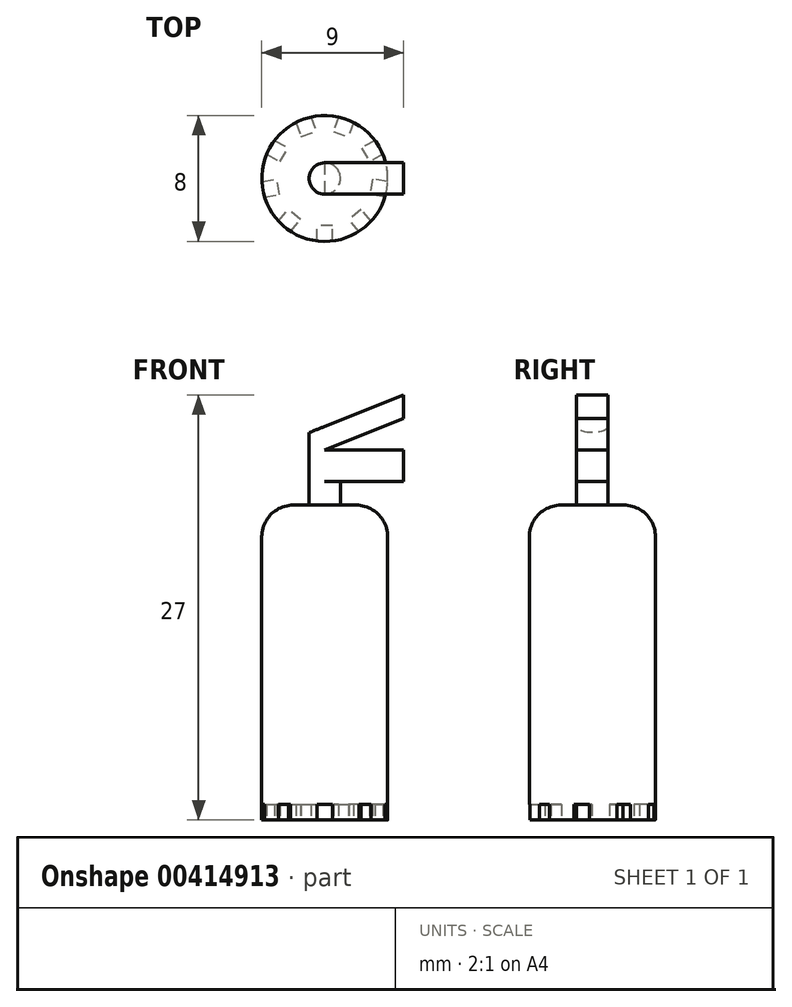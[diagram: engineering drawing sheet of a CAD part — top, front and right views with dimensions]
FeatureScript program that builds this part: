
annotation { "Feature Type Name" : "Feature", "Feature Type Description" : "" }
export const myFeature = defineFeature(function(context is Context, id is Id, definition is map)
    precondition{}
    {
        {
            var Q0;
            Q0=qCreatedBy(makeId("Top.planeOp"),FACE);
            var sketch = newSketch(context, id + "F0", { "sketchPlane" : qUnion([Q0])});
            skCircle(sketch, "E0", {"center": v(0, 0) * mm, "radius": 4 * mm});
            skSolve(sketch);
        }
        {
            var Q0;
            Q0 = qSketchRegion(id + "F0", true);
            extrude(context, id + "F1", {"entities" : qUnion([Q0]), "depth" : 20 * mm});
        }
        {
            var Q0;
            Q0=makeQuery(id+"F1.opExtrude","CAP_EDGE",EDGE,{"disambiguationData":[OSD([sQuery(id+"F0.wireOp",EDGE,"E0")])],"isStart":false});
            fillet(context, id + "F2", {"entities" : qUnion([Q0]), "radius" : 2 * mm, "tangentPropagation" : true, "allowEdgeOverflow" : false});
        }
        {
            var Q0;
            Q0=makeQuery(id+"F1.opExtrude","CAP_FACE",FACE,{"disambiguationData":[OSD([sQuery(id+"F0.wireOp",EDGE,"E0")])],"isStart":false});
            var sketch = newSketch(context, id + "F3", { "sketchPlane" : qUnion([Q0])});
            skCircle(sketch, "E1", {"center": v(0, 0) * mm, "radius": 1 * mm});
            skSolve(sketch);
        }
        {
            var Q0;
            Q0 = qSketchRegion(id + "F3", true);
            extrude(context, id + "F4", {"entities" : qUnion([Q0]), "operationType" : NewBodyOperationType.ADD, "depth" : 1.5 * mm});
        }
        {
            var Q0;
            Q0=makeQuery(id+"F4.opExtrude","CAP_FACE",FACE,{"disambiguationData":[OSD([sQuery(id+"F3.wireOp",EDGE,"E1")])],"isStart":false});
            var sketch = newSketch(context, id + "F5", { "sketchPlane" : qUnion([Q0])});
            skLineSegment(sketch, "E2", {"start": v(0, 1) * mm, "end": v(5, 1) * mm});
            skLineSegment(sketch, "E3", {"start": v(5, 1) * mm, "end": v(5, -1) * mm});
            skLineSegment(sketch, "E4", {"start": v(5, -1) * mm, "end": v(0, -1) * mm});
            skArc(sketch, "E5", {"start": v(0, 1) * mm, "mid": v(-1, 0) * mm, "end": v(0, -1) * mm});
            skSolve(sketch);
        }
        {
            var Q0;
            Q0 = qSketchRegion(id + "F5", true);
            extrude(context, id + "F6", {"entities" : qUnion([Q0]), "operationType" : NewBodyOperationType.ADD, "depth" : 2 * mm});
        }
        {
            var Q0;
            Q0=makeQuery(id+"F6.opExtrude","SWEPT_FACE",FACE,{"disambiguationData":[OSD([sQuery(id+"F5.wireOp",EDGE,"E4")])]});
            var sketch = newSketch(context, id + "F7", { "sketchPlane" : qUnion([Q0])});
            skLineSegment(sketch, "E6", {"start": v(0, 23.5) * mm, "end": v(5, 25.5) * mm});
            skLineSegment(sketch, "E7", {"start": v(5, 25.5) * mm, "end": v(5, 27) * mm});
            skLineSegment(sketch, "E8", {"start": v(5, 27) * mm, "end": v(-1, 24.6) * mm});
            skLineSegment(sketch, "E9", {"start": v(0, 23.5) * mm, "end": v(-1, 23.5) * mm});
            skLineSegment(sketch, "E10", {"start": v(-1, 23.5) * mm, "end": v(-1, 24.6) * mm});
            skSolve(sketch);
        }
        {
            var Q0;
            Q0 = qSketchRegion(id + "F7", true);
            extrude(context, id + "F8", {"entities" : qUnion([Q0]), "operationType" : NewBodyOperationType.ADD, "oppositeDirection" : true, "depth" : 2 * mm});
        }
        {
            var Q0;
            Q0=makeQuery(id+"F8.opExtrude","CAP_EDGE",EDGE,{"disambiguationData":[OSD([sQuery(id+"F7.wireOp",EDGE,"E10")])],"isStart":true});
            var Q1;
            Q1=makeQuery(id+"F8.opExtrude","CAP_EDGE",EDGE,{"disambiguationData":[OSD([sQuery(id+"F7.wireOp",EDGE,"E10")])],"isStart":false});
            fillet(context, id + "F9", {"entities" : qUnion([Q0, Q1]), "radius" : 1 * mm, "tangentPropagation" : true, "allowEdgeOverflow" : false});
        }
        {
            var Q0;
            Q0=makeQuery(id+"F1.opExtrude","CAP_FACE",FACE,{"disambiguationData":[OSD([sQuery(id+"F0.wireOp",EDGE,"E0")])],"isStart":true});
            var sketch = newSketch(context, id + "F10", { "sketchPlane" : qUnion([Q0])});
            skLineSegment(sketch, "E11", {"start": v(0, 0) * mm, "end": v(0, 4) * mm, "construction": true});
            skLineSegment(sketch, "E12", {"start": v(0, 4) * mm, "end": v(-0.5, 4) * mm});
            skLineSegment(sketch, "E13", {"start": v(-0.5, 4) * mm, "end": v(-0.5, 3) * mm});
            skLineSegment(sketch, "E14", {"start": v(0, 4) * mm, "end": v(0.5, 4) * mm});
            skLineSegment(sketch, "E15", {"start": v(0.5, 4) * mm, "end": v(0.5, 3) * mm});
            skLineSegment(sketch, "E16", {"start": v(0.5, 3) * mm, "end": v(-0.5, 3) * mm});
            skPoint(sketch, "E16.endSnap0", {"position": v(-0.5, 3.12) * mm});
            skPoint(sketch, "E17.orphan", {"position": v(-0.5, 2.23) * mm});
            skLineSegment(sketch, "E18.1.0", {"start": v(2.95, 2.74) * mm, "end": v(2.31, 1.98) * mm});
            skLineSegment(sketch, "E18.1.1", {"start": v(2.57, 3.06) * mm, "end": v(2.95, 2.74) * mm});
            skLineSegment(sketch, "E18.1.2", {"start": v(2.57, 3.06) * mm, "end": v(2.19, 3.39) * mm});
            skLineSegment(sketch, "E18.1.3", {"start": v(2.19, 3.39) * mm, "end": v(1.55, 2.62) * mm});
            skLineSegment(sketch, "E18.1.4", {"start": v(2.31, 1.98) * mm, "end": v(1.55, 2.62) * mm});
            skLineSegment(sketch, "E18.2.0", {"start": v(4.03, 0.2) * mm, "end": v(3.04, 0.03) * mm});
            skLineSegment(sketch, "E18.2.1", {"start": v(3.94, 0.7) * mm, "end": v(4.03, 0.2) * mm});
            skLineSegment(sketch, "E18.2.2", {"start": v(3.94, 0.7) * mm, "end": v(3.85, 1.19) * mm});
            skLineSegment(sketch, "E18.2.3", {"start": v(3.85, 1.19) * mm, "end": v(2.87, 1.01) * mm});
            skLineSegment(sketch, "E18.2.4", {"start": v(3.04, 0.03) * mm, "end": v(2.87, 1.01) * mm});
            skLineSegment(sketch, "E18.3.0", {"start": v(3.21, -2.43) * mm, "end": v(2.35, -1.93) * mm});
            skLineSegment(sketch, "E18.3.1", {"start": v(3.46, -2) * mm, "end": v(3.21, -2.43) * mm});
            skLineSegment(sketch, "E18.3.2", {"start": v(3.46, -2) * mm, "end": v(3.71, -1.57) * mm});
            skLineSegment(sketch, "E18.3.3", {"start": v(3.71, -1.57) * mm, "end": v(2.85, -1.07) * mm});
            skLineSegment(sketch, "E18.3.4", {"start": v(2.35, -1.93) * mm, "end": v(2.85, -1.07) * mm});
            skLineSegment(sketch, "E18.4.0", {"start": v(0.9, -3.93) * mm, "end": v(0.56, -3) * mm});
            skLineSegment(sketch, "E18.4.1", {"start": v(1.37, -3.76) * mm, "end": v(0.9, -3.93) * mm});
            skLineSegment(sketch, "E18.4.2", {"start": v(1.37, -3.76) * mm, "end": v(1.84, -3.59) * mm});
            skLineSegment(sketch, "E18.4.3", {"start": v(1.84, -3.59) * mm, "end": v(1.5, -2.65) * mm});
            skLineSegment(sketch, "E18.4.4", {"start": v(0.56, -3) * mm, "end": v(1.5, -2.65) * mm});
            skLineSegment(sketch, "E18.5.0", {"start": v(-1.84, -3.59) * mm, "end": v(-1.5, -2.65) * mm});
            skLineSegment(sketch, "E18.5.1", {"start": v(-1.37, -3.76) * mm, "end": v(-1.84, -3.59) * mm});
            skLineSegment(sketch, "E18.5.2", {"start": v(-1.37, -3.76) * mm, "end": v(-0.9, -3.93) * mm});
            skLineSegment(sketch, "E18.5.3", {"start": v(-0.9, -3.93) * mm, "end": v(-0.56, -3) * mm});
            skLineSegment(sketch, "E18.5.4", {"start": v(-1.5, -2.65) * mm, "end": v(-0.56, -3) * mm});
            skLineSegment(sketch, "E18.6.0", {"start": v(-3.71, -1.57) * mm, "end": v(-2.85, -1.07) * mm});
            skLineSegment(sketch, "E18.6.1", {"start": v(-3.46, -2) * mm, "end": v(-3.71, -1.57) * mm});
            skLineSegment(sketch, "E18.6.2", {"start": v(-3.46, -2) * mm, "end": v(-3.21, -2.43) * mm});
            skLineSegment(sketch, "E18.6.3", {"start": v(-3.21, -2.43) * mm, "end": v(-2.35, -1.93) * mm});
            skLineSegment(sketch, "E18.6.4", {"start": v(-2.85, -1.07) * mm, "end": v(-2.35, -1.93) * mm});
            skLineSegment(sketch, "E18.7.0", {"start": v(-3.85, 1.19) * mm, "end": v(-2.87, 1.01) * mm});
            skLineSegment(sketch, "E18.7.1", {"start": v(-3.94, 0.7) * mm, "end": v(-3.85, 1.19) * mm});
            skLineSegment(sketch, "E18.7.2", {"start": v(-3.94, 0.7) * mm, "end": v(-4.03, 0.2) * mm});
            skLineSegment(sketch, "E18.7.3", {"start": v(-4.03, 0.2) * mm, "end": v(-3.04, 0.03) * mm});
            skLineSegment(sketch, "E18.7.4", {"start": v(-2.87, 1.01) * mm, "end": v(-3.04, 0.03) * mm});
            skLineSegment(sketch, "E18.8.0", {"start": v(-2.19, 3.39) * mm, "end": v(-1.55, 2.62) * mm});
            skLineSegment(sketch, "E18.8.1", {"start": v(-2.57, 3.06) * mm, "end": v(-2.19, 3.39) * mm});
            skLineSegment(sketch, "E18.8.2", {"start": v(-2.57, 3.06) * mm, "end": v(-2.95, 2.74) * mm});
            skLineSegment(sketch, "E18.8.3", {"start": v(-2.95, 2.74) * mm, "end": v(-2.31, 1.98) * mm});
            skLineSegment(sketch, "E18.8.4", {"start": v(-1.55, 2.62) * mm, "end": v(-2.31, 1.98) * mm});
            skPoint(sketch, "E18.center", {"position": v(0, 0) * mm});
            skLineSegment(sketch, "E18.anchor1", {"start": v(0, 0) * mm, "end": v(0.5, 3) * mm, "construction": true});
            skLineSegment(sketch, "E18.anchor2", {"start": v(0, 0) * mm, "end": v(0.5, 3) * mm, "construction": true});
            skSolve(sketch);
        }
        {
            var Q0;
            Q0 = qSketchRegion(id + "F10", true);
            extrude(context, id + "F11", {"entities" : qUnion([Q0]), "operationType" : NewBodyOperationType.REMOVE, "oppositeDirection" : true, "depth" : 1 * mm});
        }
    });
